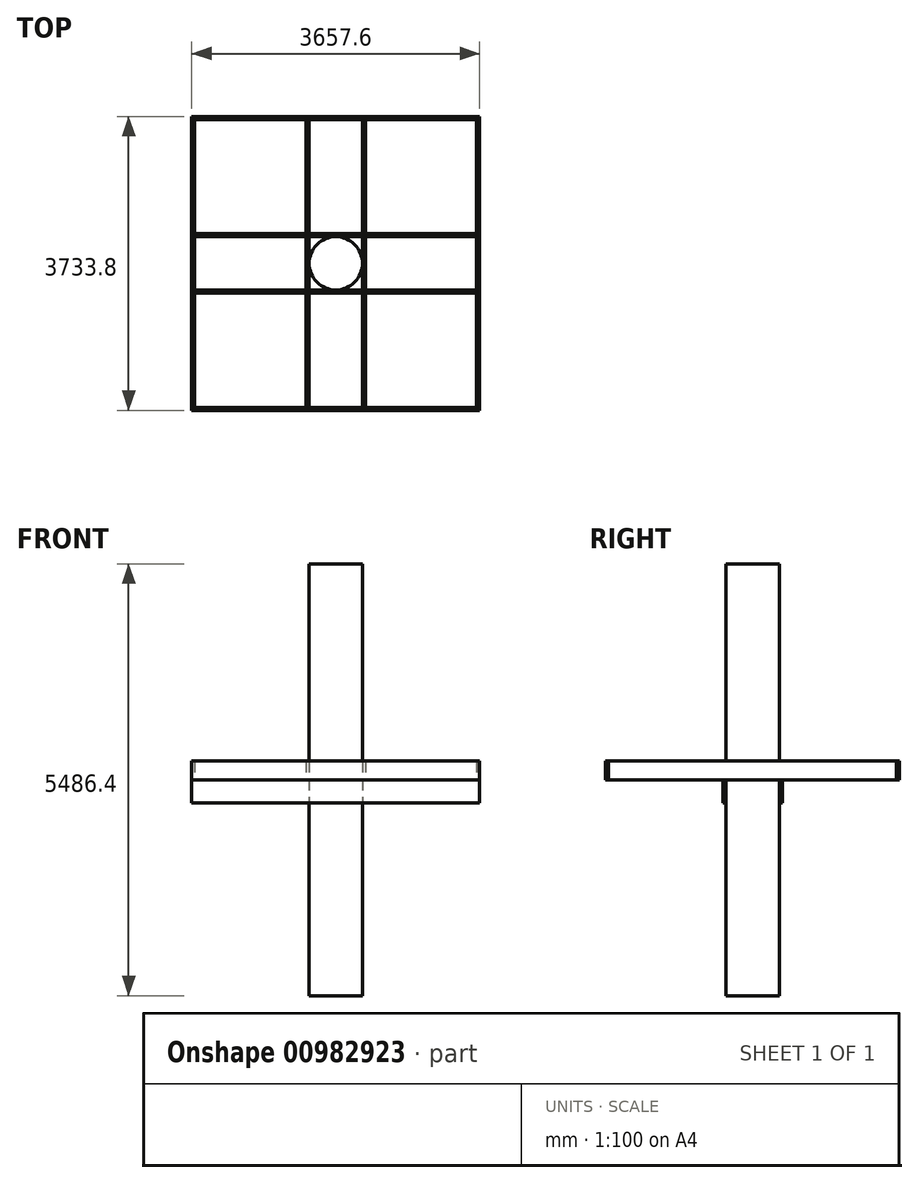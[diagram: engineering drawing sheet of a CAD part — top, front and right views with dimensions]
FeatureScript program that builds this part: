
annotation { "Feature Type Name" : "Feature", "Feature Type Description" : "" }
export const myFeature = defineFeature(function(context is Context, id is Id, definition is map)
    precondition{}
    {
        {
            var Q0;
            Q0=qCreatedBy(makeId("Top.planeOp"),FACE);
            var sketch = newSketch(context, id + "F0", { "sketchPlane" : qUnion([Q0])});
            skCircle(sketch, "E0", {"center": v(0, 0) * mm, "radius": 338.45 * mm});
            skLineSegment(sketch, "E1", {"start": v(0, -338.45) * mm, "end": v(0, -357.5) * mm, "construction": true});
            skLineSegment(sketch, "E2", {"start": v(0, 338.45) * mm, "end": v(0, 357.5) * mm, "construction": true});
            skLineSegment(sketch, "E3.bottom", {"start": v(1828.8, 338.46) * mm, "end": v(-1828.8, 338.45) * mm});
            skLineSegment(sketch, "E3.top", {"start": v(1828.8, 376.56) * mm, "end": v(-1828.8, 376.55) * mm});
            skLineSegment(sketch, "E3.left", {"start": v(1828.8, 338.46) * mm, "end": v(1828.8, 376.56) * mm});
            skLineSegment(sketch, "E3.right", {"start": v(-1828.8, 338.45) * mm, "end": v(-1828.8, 376.55) * mm});
            skPoint(sketch, "E3.middle", {"position": v(0, 357.5) * mm});
            skLineSegment(sketch, "E4.bottom", {"start": v(1828.8, -338.46) * mm, "end": v(-1828.8, -338.45) * mm});
            skLineSegment(sketch, "E4.top", {"start": v(1828.8, -376.56) * mm, "end": v(-1828.8, -376.55) * mm});
            skLineSegment(sketch, "E4.left", {"start": v(1828.8, -338.46) * mm, "end": v(1828.8, -376.56) * mm});
            skLineSegment(sketch, "E4.right", {"start": v(-1828.8, -338.45) * mm, "end": v(-1828.8, -376.55) * mm});
            skPoint(sketch, "E4.middle", {"position": v(0, -357.5) * mm});
            skSolve(sketch);
        }
        {
            var Q0;
            {var subQ0=sQuery(id+"F0.wireOp",EDGE,"E0");var subQ1=makeQuery(id+"F0.imprint","INTERSECT",VERTEX,{"derivedFrom":[subQ0,sQuery(id+"F0.wireOp",EDGE,"E3.bottom")]});Q0=makeQuery(id+"F0.imprint","IMPRINT",FACE,{"disambiguationData":[TD([[makeQuery(id+"F0.imprint","IMPRINT",EDGE,{"disambiguationData":[TD([[subQ1,-1.0]])],"derivedFrom":subQ0}),1.0]])]});}
            extrude(context, id + "F1", {"entities" : qUnion([Q0]), "endBound" : BoundingType.SYMMETRIC, "depth" : 5486.4 * mm, "offsetDistance" : 25 * mm});
        }
        {
            var Q0;
            Q0=makeQuery(id+"F0.imprint","IMPRINT",FACE,{"disambiguationData":[TD([[makeQuery(id+"F0.imprint","IMPRINT",EDGE,{"derivedFrom":sQuery(id+"F0.wireOp",EDGE,"E4.top")}),-1.0]])]});
            var Q1;
            Q1=makeQuery(id+"F0.imprint","IMPRINT",FACE,{"disambiguationData":[TD([[makeQuery(id+"F0.imprint","IMPRINT",EDGE,{"derivedFrom":sQuery(id+"F0.wireOp",EDGE,"E3.top")}),1.0]])]});
            extrude(context, id + "F2", {"entities" : qUnion([Q0, Q1]), "oppositeDirection" : true, "depth" : 292.1 * mm, "offsetDistance" : 25 * mm});
        }
        {
            var Q0;
            Q0=qCreatedBy(makeId("Top.planeOp"),FACE);
            var sketch = newSketch(context, id + "F3", { "sketchPlane" : qUnion([Q0])});
            skCircle(sketch, "E5.0", {"center": v(0, 0) * mm, "radius": 338.45 * mm});
            skLineSegment(sketch, "E6", {"start": v(0, 0) * mm, "end": v(1809.75, 0) * mm, "construction": true});
            skLineSegment(sketch, "E7", {"start": v(-338.45, 0) * mm, "end": v(-357.5, 0) * mm, "construction": true});
            skLineSegment(sketch, "E8.bottom", {"start": v(-338.45, 1828.8) * mm, "end": v(-376.55, 1828.8) * mm});
            skLineSegment(sketch, "E8.top", {"start": v(-338.45, -1828.8) * mm, "end": v(-376.55, -1828.8) * mm});
            skLineSegment(sketch, "E8.left", {"start": v(-338.45, 1828.8) * mm, "end": v(-338.45, -1828.8) * mm});
            skLineSegment(sketch, "E8.right", {"start": v(-376.55, 1828.8) * mm, "end": v(-376.55, -1828.8) * mm});
            skPoint(sketch, "E8.middle", {"position": v(-357.5, 0) * mm});
            skLineSegment(sketch, "E9", {"start": v(0, 338.45) * mm, "end": v(0, -338.45) * mm, "construction": true});
            skLineSegment(sketch, "E10.MirrorCS", {"start": v(338.45, 1828.8) * mm, "end": v(376.55, 1828.8) * mm});
            skLineSegment(sketch, "E11.MirrorCS", {"start": v(338.45, -1828.8) * mm, "end": v(376.55, -1828.8) * mm});
            skLineSegment(sketch, "E12.MirrorCS", {"start": v(338.45, 1828.8) * mm, "end": v(338.45, -1828.8) * mm});
            skLineSegment(sketch, "E13.MirrorCS", {"start": v(376.55, 1828.8) * mm, "end": v(376.55, -1828.8) * mm});
            skLineSegment(sketch, "E14.bottom", {"start": v(1790.7, 1828.8) * mm, "end": v(1828.8, 1828.8) * mm});
            skLineSegment(sketch, "E14.top", {"start": v(1790.7, -1828.8) * mm, "end": v(1828.8, -1828.8) * mm});
            skLineSegment(sketch, "E14.left", {"start": v(1790.7, 1828.8) * mm, "end": v(1790.7, -1828.8) * mm});
            skLineSegment(sketch, "E14.right", {"start": v(1828.8, 1828.8) * mm, "end": v(1828.8, -1828.8) * mm});
            skPoint(sketch, "E14.middle", {"position": v(1809.75, 0) * mm});
            skLineSegment(sketch, "E15.MirrorCS", {"start": v(-1790.7, 1828.8) * mm, "end": v(-1828.8, 1828.8) * mm});
            skLineSegment(sketch, "E16.MirrorCS", {"start": v(-1790.7, -1828.8) * mm, "end": v(-1828.8, -1828.8) * mm});
            skLineSegment(sketch, "E17.MirrorCS", {"start": v(-1790.7, 1828.8) * mm, "end": v(-1790.7, -1828.8) * mm});
            skLineSegment(sketch, "E18.MirrorCS", {"start": v(-1828.8, 1828.8) * mm, "end": v(-1828.8, -1828.8) * mm});
            skLineSegment(sketch, "E19.bottom", {"start": v(-1828.8, 1828.8) * mm, "end": v(1828.8, 1828.8) * mm});
            skLineSegment(sketch, "E19.top", {"start": v(-1828.8, 1866.9) * mm, "end": v(1828.8, 1866.9) * mm});
            skLineSegment(sketch, "E19.left", {"start": v(-1828.8, 1828.8) * mm, "end": v(-1828.8, 1866.9) * mm});
            skLineSegment(sketch, "E19.right", {"start": v(1828.8, 1828.8) * mm, "end": v(1828.8, 1866.9) * mm});
            skLineSegment(sketch, "E20.bottom", {"start": v(-1828.8, -1828.8) * mm, "end": v(1828.8, -1828.8) * mm});
            skLineSegment(sketch, "E20.top", {"start": v(-1828.8, -1866.9) * mm, "end": v(1828.8, -1866.9) * mm});
            skLineSegment(sketch, "E20.left", {"start": v(-1828.8, -1828.8) * mm, "end": v(-1828.8, -1866.9) * mm});
            skLineSegment(sketch, "E20.right", {"start": v(1828.8, -1828.8) * mm, "end": v(1828.8, -1866.9) * mm});
            skSolve(sketch);
        }
        {
            var Q0;
            {var subQ0=sQuery(id+"F3.wireOp",EDGE,"E17.MirrorCS");Q0=makeQuery(id+"F3.imprint","IMPRINT",FACE,{"disambiguationData":[TD([[makeQuery(id+"F3.imprint","IMPRINT",EDGE,{"derivedFrom":subQ0}),-1.0]])]});}
            var Q1;
            {var subQ3=sQuery(id+"F3.wireOp",EDGE,"E8.right");Q1=makeQuery(id+"F3.imprint","IMPRINT",FACE,{"disambiguationData":[TD([[makeQuery(id+"F3.imprint","IMPRINT",EDGE,{"derivedFrom":subQ3}),1.0]])]});}
            var Q2;
            {var subQ0=sQuery(id+"F3.wireOp",EDGE,"E13.MirrorCS");Q2=makeQuery(id+"F3.imprint","IMPRINT",FACE,{"disambiguationData":[TD([[makeQuery(id+"F3.imprint","IMPRINT",EDGE,{"derivedFrom":subQ0}),-1.0]])]});}
            var Q3;
            {var subQ0=sQuery(id+"F3.wireOp",EDGE,"E14.left");Q3=makeQuery(id+"F3.imprint","IMPRINT",FACE,{"disambiguationData":[TD([[makeQuery(id+"F3.imprint","IMPRINT",EDGE,{"derivedFrom":subQ0}),1.0]])]});}
            extrude(context, id + "F4", {"entities" : qUnion([Q0, Q1, Q2, Q3]), "depth" : 241.3 * mm, "offsetDistance" : 25 * mm});
        }
        {
            var Q0;
            Q0=makeQuery(id+"F3.imprint","IMPRINT",FACE,{"disambiguationData":[TD([[makeQuery(id+"F3.imprint","IMPRINT",EDGE,{"derivedFrom":sQuery(id+"F3.wireOp",EDGE,"E20.top")}),1.0]])]});
            var Q1;
            Q1=makeQuery(id+"F3.imprint","IMPRINT",FACE,{"disambiguationData":[TD([[makeQuery(id+"F3.imprint","IMPRINT",EDGE,{"derivedFrom":sQuery(id+"F3.wireOp",EDGE,"E19.top")}),-1.0]])]});
            extrude(context, id + "F5", {"entities" : qUnion([Q0, Q1]), "depth" : 241.3 * mm, "offsetDistance" : 25 * mm});
        }
    });
